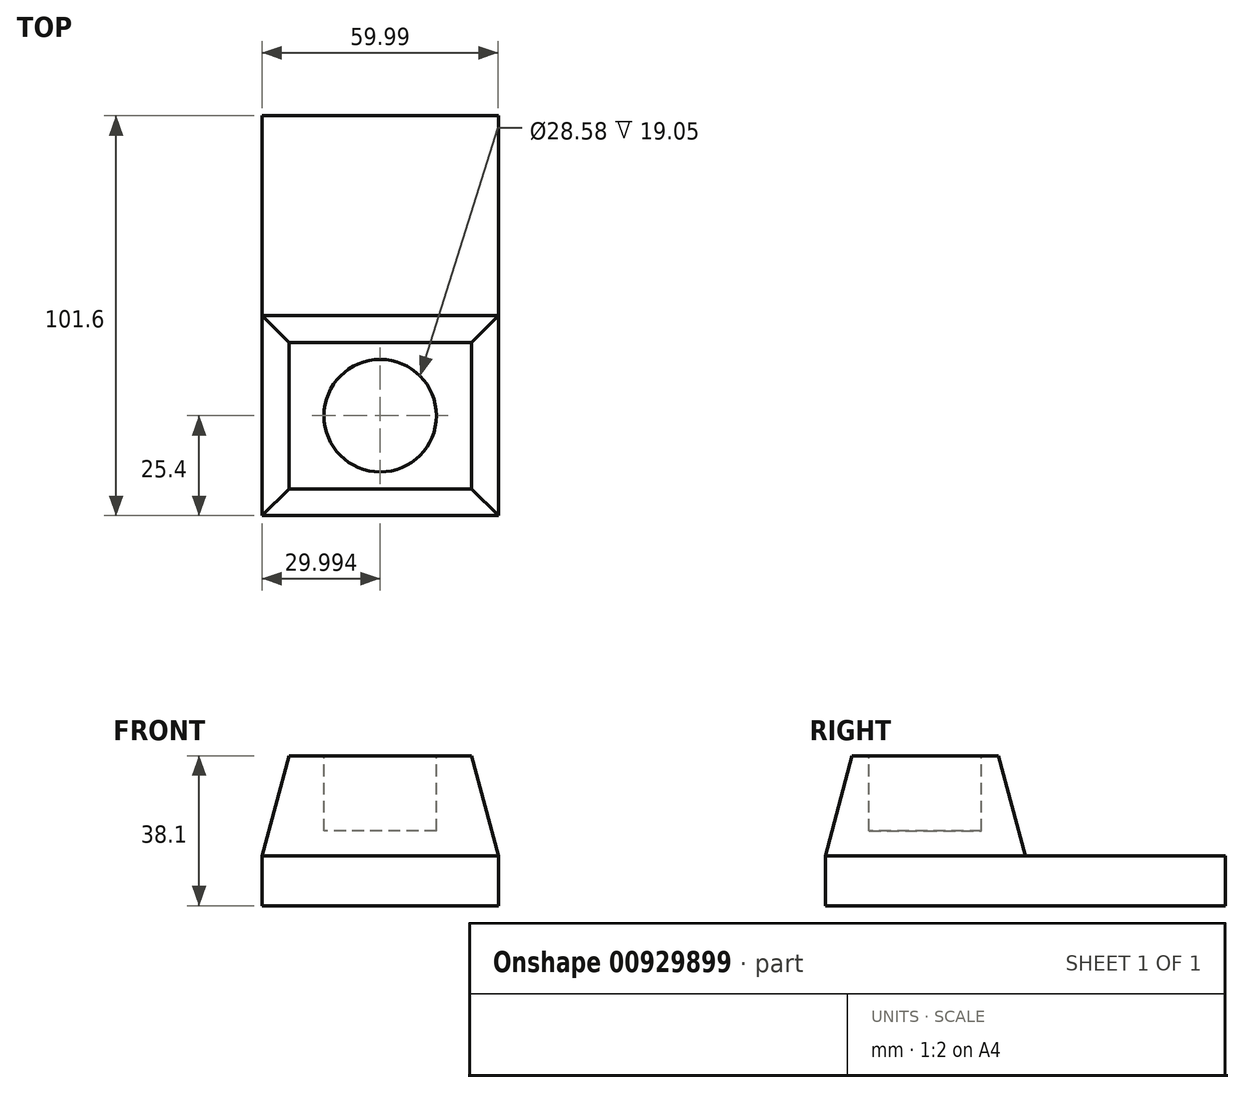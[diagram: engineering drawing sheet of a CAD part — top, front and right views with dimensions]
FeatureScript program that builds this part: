
annotation { "Feature Type Name" : "Feature", "Feature Type Description" : "" }
export const myFeature = defineFeature(function(context is Context, id is Id, definition is map)
    precondition{}
    {
        {
            var Q0;
            Q0=qCreatedBy(makeId("Front.planeOp"),FACE);
            var sketch = newSketch(context, id + "F0", { "sketchPlane" : qUnion([Q0])});
            skLineSegment(sketch, "E0.bottom", {"start": v(-27, -1.96) * mm, "end": v(33, -1.96) * mm});
            skLineSegment(sketch, "E0.top", {"start": v(-27, -14.66) * mm, "end": v(33, -14.66) * mm});
            skLineSegment(sketch, "E0.left", {"start": v(-27, -1.96) * mm, "end": v(-27, -14.66) * mm});
            skLineSegment(sketch, "E0.right", {"start": v(33, -1.96) * mm, "end": v(33, -14.66) * mm});
            skSolve(sketch);
        }
        {
            var Q0;
            Q0 = qSketchRegion(id + "F0", true);
            extrude(context, id + "F1", {"entities" : qUnion([Q0]), "depth" : 101.6 * mm, "offsetDistance" : 25.4 * mm});
        }
        {
            var Q0;
            Q0=makeQuery(id+"F1.opExtrude","SWEPT_FACE",FACE,{"disambiguationData":[OSD([sQuery(id+"F0.wireOp",EDGE,"E0.bottom")])]});
            var sketch = newSketch(context, id + "F2", { "sketchPlane" : qUnion([Q0])});
            skLineSegment(sketch, "E1.bottom", {"start": v(-27, 0) * mm, "end": v(33, 0) * mm});
            skLineSegment(sketch, "E1.top", {"start": v(-27, -50.8) * mm, "end": v(33, -50.8) * mm});
            skLineSegment(sketch, "E1.left", {"start": v(-27, 0) * mm, "end": v(-27, -50.8) * mm});
            skLineSegment(sketch, "E1.right", {"start": v(33, 0) * mm, "end": v(33, -50.8) * mm});
            skSolve(sketch);
        }
        {
            var Q0;
            {var subQ0=sQuery(id+"F2.wireOp",EDGE,"E1.top");Q0=makeQuery(id+"F2.imprint","IMPRINT",FACE,{"disambiguationData":[TD([[makeQuery(id+"F2.imprint","IMPRINT",EDGE,{"derivedFrom":subQ0}),-1.0]])]});}
            extrude(context, id + "F3", {"entities" : qUnion([Q0]), "operationType" : NewBodyOperationType.ADD, "depth" : 25.4 * mm, "offsetDistance" : 25.4 * mm, "hasDraft" : true, "draftAngle" : 15 * degree, "draftPullDirection" : true});
        }
        {
            var Q0;
            Q0=makeQuery(id+"F3.opExtrude","CAP_FACE",FACE,{"disambiguationData":[OSD([sQuery(id+"F0.wireOp",EDGE,"E0.bottom"),sQuery(id+"F0.wireOp",EDGE,"E0.left"),sQuery(id+"F0.wireOp",EDGE,"E0.right"),sQuery(id+"F2.wireOp",EDGE,"E1.top")])],"isStart":false});
            var sketch = newSketch(context, id + "F4", { "sketchPlane" : qUnion([Q0])});
            skCircle(sketch, "E2", {"center": v(3, -76.2) * mm, "radius": 14.3 * mm});
            skPoint(sketch, "E2.centerSnap0", {"position": v(26.19, -76.2) * mm});
            skPoint(sketch, "E2.centerSnap1", {"position": v(3, -57.6) * mm});
            skSolve(sketch);
        }
        {
            var Q0;
            Q0=makeQuery(id+"F4.imprint","IMPRINT",FACE,{"disambiguationData":[TD([[makeQuery(id+"F4.imprint","IMPRINT",EDGE,{"derivedFrom":sQuery(id+"F4.wireOp",EDGE,"E2")}),1.0]])]});
            extrude(context, id + "F5", {"entities" : qUnion([Q0]), "operationType" : NewBodyOperationType.REMOVE, "oppositeDirection" : true, "depth" : 19.05 * mm, "offsetDistance" : 25.4 * mm});
        }
    });
